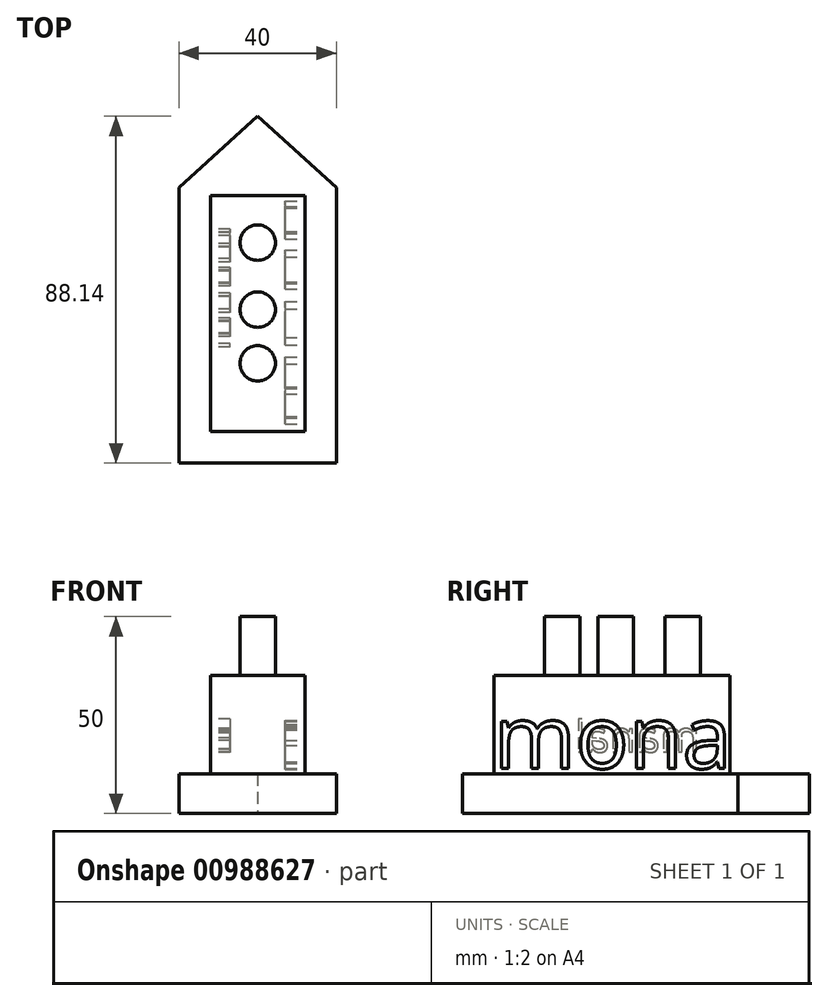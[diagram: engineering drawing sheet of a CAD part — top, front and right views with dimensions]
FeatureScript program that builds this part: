
annotation { "Feature Type Name" : "Feature", "Feature Type Description" : "" }
export const myFeature = defineFeature(function(context is Context, id is Id, definition is map)
    precondition{}
    {
        {
            var Q0;
            Q0=qCreatedBy(makeId("Top.planeOp"),FACE);
            var sketch = newSketch(context, id + "F0", { "sketchPlane" : qUnion([Q0])});
            skLineSegment(sketch, "E0", {"start": v(-59, 40.6) * mm, "end": v(-59, -29.4) * mm});
            skLineSegment(sketch, "E1", {"start": v(-59, -29.4) * mm, "end": v(-19, -29.4) * mm});
            skLineSegment(sketch, "E2", {"start": v(-19, 40.6) * mm, "end": v(-19, -29.4) * mm});
            skLineSegment(sketch, "E3", {"start": v(-59, 40.6) * mm, "end": v(-39, 58.73) * mm});
            skLineSegment(sketch, "E4", {"start": v(-39, 58.73) * mm, "end": v(-19, 40.6) * mm});
            skPoint(sketch, "E5.orphan", {"position": v(-19, -42.94) * mm});
            skSolve(sketch);
        }
        {
            var Q0;
            Q0=makeQuery(id+"F0.imprint","IMPRINT",FACE,{"disambiguationData":[TD([[makeQuery(id+"F0.imprint","IMPRINT",EDGE,{"derivedFrom":sQuery(id+"F0.wireOp",EDGE,"E0")}),1.0]])]});
            extrude(context, id + "F1", {"entities" : qUnion([Q0]), "depth" : 10 * mm, "offsetDistance" : 25 * mm});
        }
        {
            var Q0;
            Q0=makeQuery(id+"F1.opExtrude","CAP_FACE",FACE,{"disambiguationData":[OSD([sQuery(id+"F0.wireOp",EDGE,"E0"),sQuery(id+"F0.wireOp",EDGE,"E1"),sQuery(id+"F0.wireOp",EDGE,"E2"),sQuery(id+"F0.wireOp",EDGE,"E3"),sQuery(id+"F0.wireOp",EDGE,"E4")])],"isStart":false});
            var sketch = newSketch(context, id + "F2", { "sketchPlane" : qUnion([Q0])});
            skLineSegment(sketch, "E6", {"start": v(-51, 38.6) * mm, "end": v(-27, 38.6) * mm});
            skLineSegment(sketch, "E7", {"start": v(-27, 38.6) * mm, "end": v(-27, -21.4) * mm});
            skLineSegment(sketch, "E8", {"start": v(-27, -21.4) * mm, "end": v(-51, -21.4) * mm});
            skLineSegment(sketch, "E9", {"start": v(-51, 38.6) * mm, "end": v(-51, -21.4) * mm});
            skSolve(sketch);
        }
        {
            var Q0;
            Q0 = qSketchRegion(id + "F2", true);
            extrude(context, id + "F3", {"entities" : qUnion([Q0]), "operationType" : NewBodyOperationType.ADD, "depth" : 25 * mm, "offsetDistance" : 25 * mm});
        }
        {
            var Q0;
            Q0=makeQuery(id+"F3.opExtrude","CAP_FACE",FACE,{"disambiguationData":[OSD([sQuery(id+"F2.wireOp",EDGE,"E6"),sQuery(id+"F2.wireOp",EDGE,"E7"),sQuery(id+"F2.wireOp",EDGE,"E8"),sQuery(id+"F2.wireOp",EDGE,"E9")])],"isStart":false});
            var sketch = newSketch(context, id + "F4", { "sketchPlane" : qUnion([Q0])});
            skCircle(sketch, "E10", {"center": v(-39, 26.6) * mm, "radius": 4.5 * mm});
            skCircle(sketch, "E11", {"center": v(-39, 9.57) * mm, "radius": 4.5 * mm});
            skCircle(sketch, "E12", {"center": v(-39, -4.08) * mm, "radius": 4.5 * mm});
            skSolve(sketch);
        }
        {
            var Q0;
            Q0 = qSketchRegion(id + "F4", true);
            extrude(context, id + "F5", {"entities" : qUnion([Q0]), "operationType" : NewBodyOperationType.ADD, "depth" : 15 * mm, "offsetDistance" : 25 * mm});
        }
        {
            var Q0;
            Q0=makeQuery(id+"F3.opExtrude","SWEPT_FACE",FACE,{"disambiguationData":[OSD([sQuery(id+"F2.wireOp",EDGE,"E9")])]});
            var sketch = newSketch(context, id + "F6", { "sketchPlane" : qUnion([Q0])});
            skText(sketch, "E13", { "text": "manal", "fontName": "OpenSans-Regular.ttf"});
            const initialGuessF6  = {"E13": [-0.03101, 0.0156, 1, 0, 0.0079]};
            skSetInitialGuess(sketch, initialGuessF6);
            skSolve(sketch);
        }
        {
            var Q0;
            Q0 = qSketchRegion(id + "F6", true);
            extrude(context, id + "F7", {"entities" : qUnion([Q0]), "operationType" : NewBodyOperationType.REMOVE, "oppositeDirection" : true, "depth" : 5 * mm, "offsetDistance" : 25 * mm});
        }
        {
            var Q0;
            Q0=makeQuery(id+"F3.opExtrude","SWEPT_FACE",FACE,{"disambiguationData":[OSD([sQuery(id+"F2.wireOp",EDGE,"E7")])]});
            var sketch = newSketch(context, id + "F8", { "sketchPlane" : qUnion([Q0])});
            skText(sketch, "E14", { "text": "mona", "fontName": "OpenSans-Regular.ttf"});
            const initialGuessF8  = {"E14": [-0.0214, 0.01142, 1, 0, 0.01607]};
            skSetInitialGuess(sketch, initialGuessF8);
            skSolve(sketch);
        }
        {
            var Q0;
            Q0 = qSketchRegion(id + "F8", true);
            extrude(context, id + "F9", {"entities" : qUnion([Q0]), "operationType" : NewBodyOperationType.REMOVE, "oppositeDirection" : true, "depth" : 5 * mm, "offsetDistance" : 25 * mm});
        }
    });
